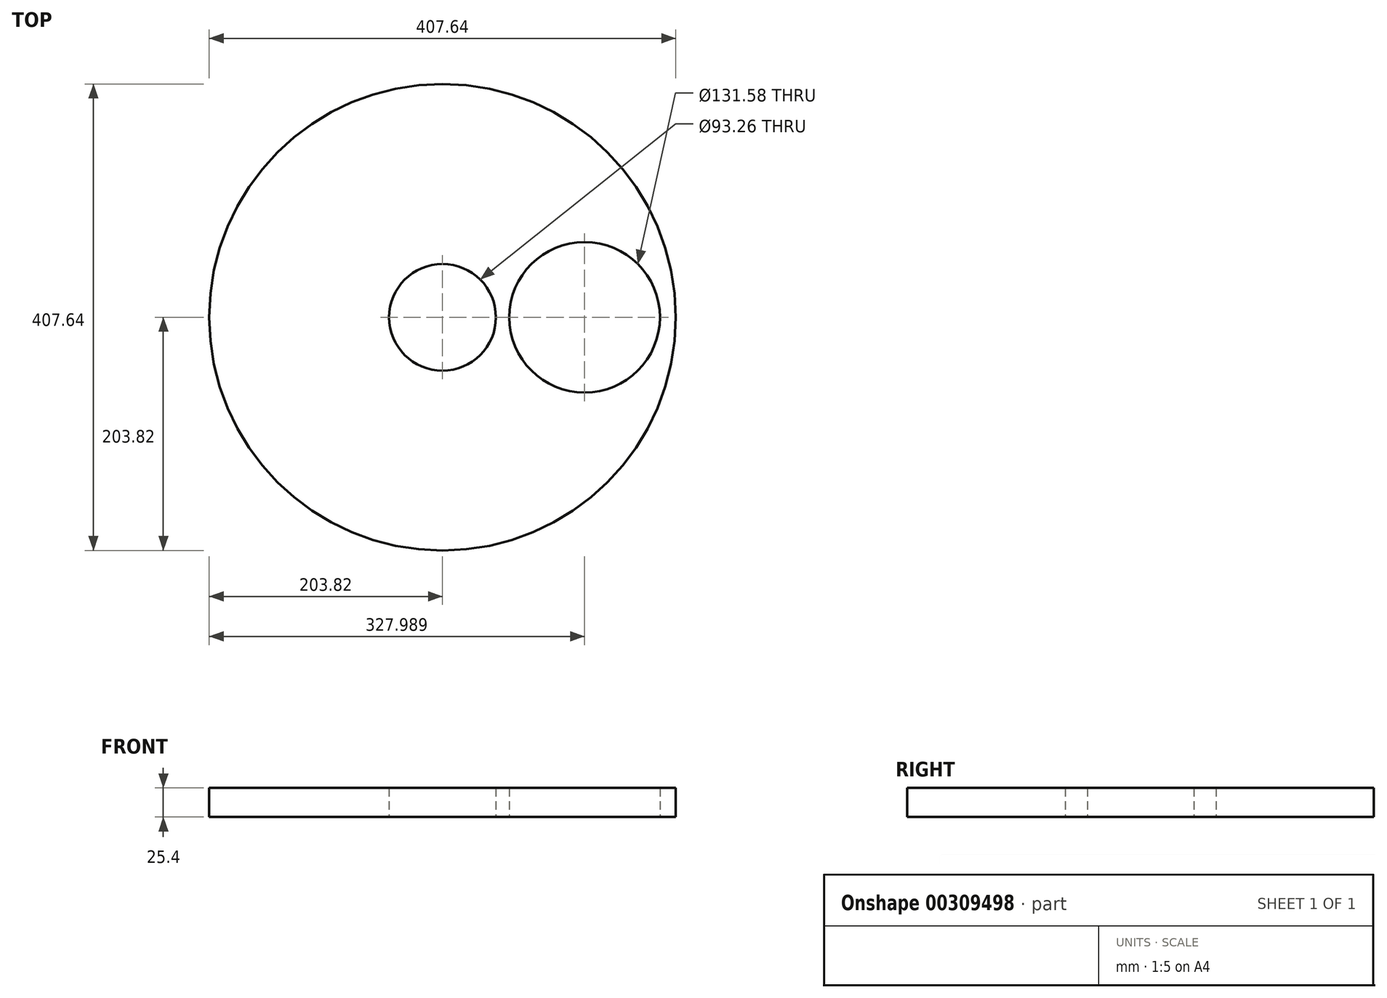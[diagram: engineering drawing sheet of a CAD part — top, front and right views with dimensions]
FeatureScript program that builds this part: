
annotation { "Feature Type Name" : "Feature", "Feature Type Description" : "" }
export const myFeature = defineFeature(function(context is Context, id is Id, definition is map)
    precondition{}
    {
        {
            var Q0;
            Q0=qCreatedBy(makeId("Top.planeOp"),FACE);
            var sketch = newSketch(context, id + "F0", { "sketchPlane" : qUnion([Q0])});
            skCircle(sketch, "E0", {"center": v(0, 0) * mm, "radius": 203.82 * mm});
            skCircle(sketch, "E1", {"center": v(124.17, 0) * mm, "radius": 65.79 * mm});
            skCircle(sketch, "E2", {"center": v(0, 0) * mm, "radius": 46.63 * mm});
            skSolve(sketch);
        }
        {
            var Q0;
            Q0=makeQuery(id+"F0.imprint","IMPRINT",FACE,{"disambiguationData":[TD([[makeQuery(id+"F0.imprint","IMPRINT",EDGE,{"derivedFrom":sQuery(id+"F0.wireOp",EDGE,"E0")}),1.0]])]});
            extrude(context, id + "F1", {"entities" : qUnion([Q0]), "depth" : 25.4 * mm});
        }
    });
